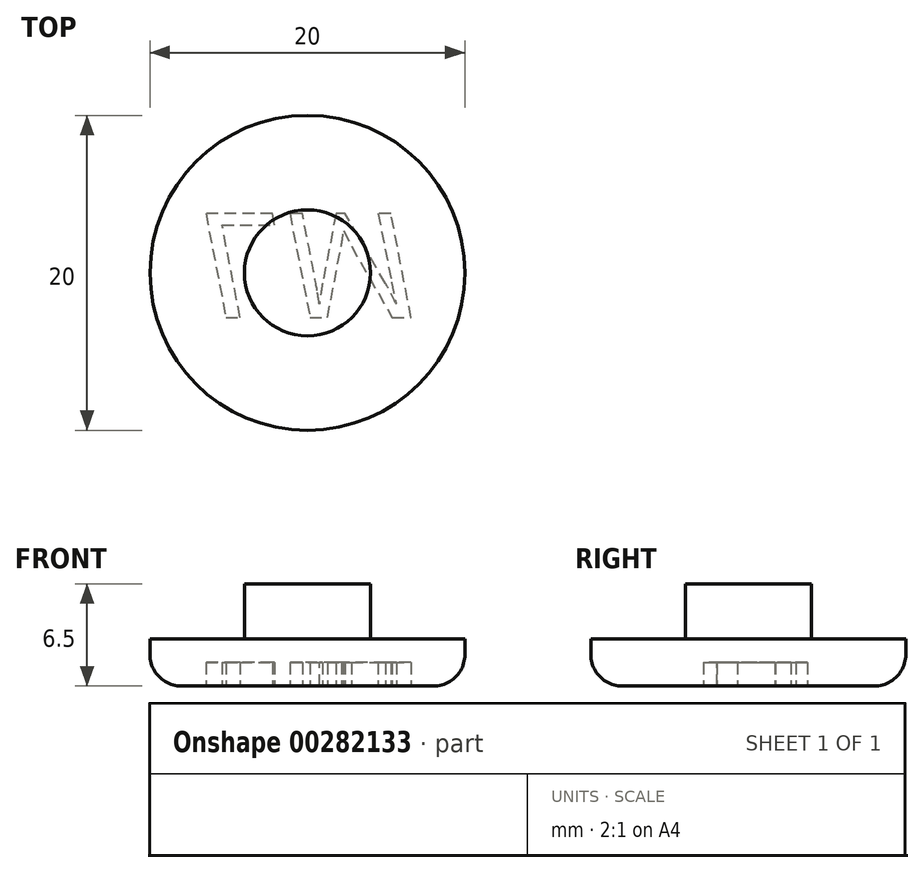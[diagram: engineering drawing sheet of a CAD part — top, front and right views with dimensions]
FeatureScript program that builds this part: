
annotation { "Feature Type Name" : "Feature", "Feature Type Description" : "" }
export const myFeature = defineFeature(function(context is Context, id is Id, definition is map)
    precondition{}
    {
        {
            var Q0;
            Q0=qCreatedBy(makeId("Top.planeOp"),FACE);
            var sketch = newSketch(context, id + "F0", { "sketchPlane" : qUnion([Q0])});
            skCircle(sketch, "E0", {"center": v(0, 0) * mm, "radius": 10 * mm});
            skSolve(sketch);
        }
        {
            var Q0;
            Q0=qSketchRegion(id+"F0",true);
            extrude(context, id + "F1", {"entities" : qUnion([Q0]), "depth" : 3 * mm});
        }
        {
            var Q0;
            Q0=makeQuery(id+"F1.opExtrude","CAP_FACE",FACE,{"disambiguationData":[OSD([sQuery(id+"F0.wireOp",EDGE,"E0")])],"isStart":false});
            var sketch = newSketch(context, id + "F2", { "sketchPlane" : qUnion([Q0])});
            skCircle(sketch, "E1", {"center": v(0, 0) * mm, "radius": 4 * mm});
            skSolve(sketch);
        }
        {
            var Q0;
            Q0=qSketchRegion(id+"F2",true);
            extrude(context, id + "F3", {"entities" : qUnion([Q0]), "operationType" : NewBodyOperationType.ADD, "depth" : 3.5 * mm});
        }
        {
            var Q0;
            Q0=makeQuery(id+"F1.opExtrude","CAP_EDGE",EDGE,{"disambiguationData":[OSD([sQuery(id+"F0.wireOp",EDGE,"E0")])],"isStart":true});
            fillet(context, id + "F4", {"entities" : qUnion([Q0]), "radius" : 2 * mm, "tangentPropagation" : true, "allowEdgeOverflow" : false});
        }
        {
            var Q0;
            Q0=makeQuery(id+"F1.opExtrude","CAP_FACE",FACE,{"disambiguationData":[OSD([sQuery(id+"F0.wireOp",EDGE,"E0")])],"isStart":true});
            var sketch = newSketch(context, id + "F5", { "sketchPlane" : qUnion([Q0])});
            skText(sketch, "E2", { "text": "LM\n", "fontName": "Arimo-Italic.ttf"});
            const initialGuessF5  = {"E2": [-0.00675, -0.00376, 1, 0, 0.00691]};
            skSetInitialGuess(sketch, initialGuessF5);
            skSolve(sketch);
        }
        {
            var Q0;
            Q0=qSketchRegion(id+"F5",true);
            extrude(context, id + "F6", {"entities" : qUnion([Q0]), "operationType" : NewBodyOperationType.REMOVE, "oppositeDirection" : true, "depth" : 1.5 * mm});
        }
    });
